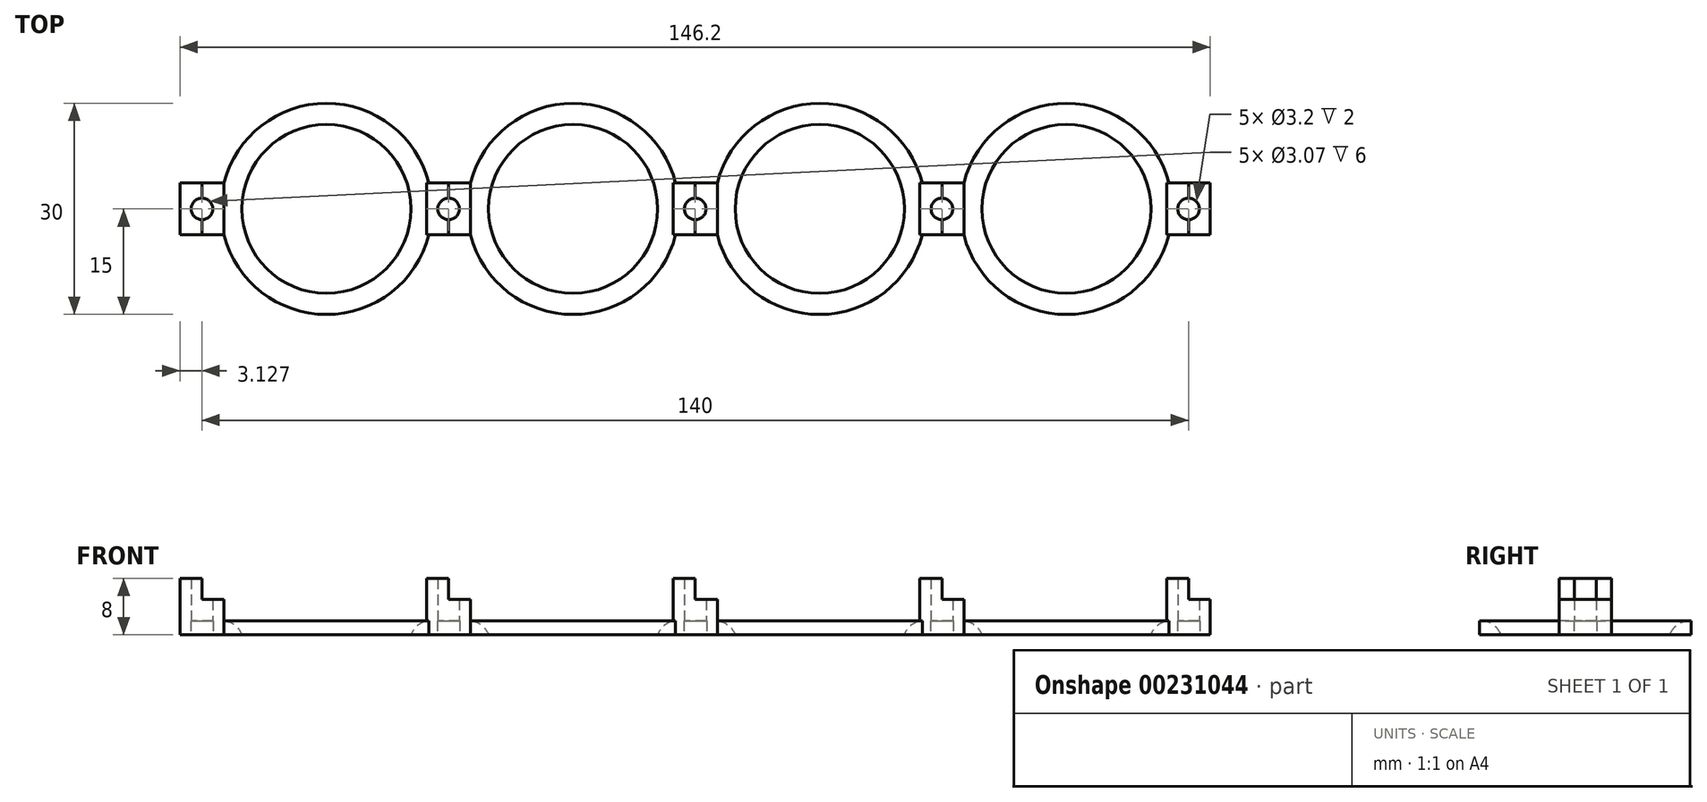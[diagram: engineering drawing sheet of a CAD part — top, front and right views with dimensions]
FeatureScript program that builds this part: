
annotation { "Feature Type Name" : "Feature", "Feature Type Description" : "" }
export const myFeature = defineFeature(function(context is Context, id is Id, definition is map)
    precondition{}
    {
        {
            var Q0;
            Q0=qCreatedBy(makeId("Top.planeOp"),FACE);
            var sketch = newSketch(context, id + "F0", { "sketchPlane" : qUnion([Q0])});
            skCircle(sketch, "E0", {"center": v(0, 0) * mm, "radius": 12 * mm});
            skArc(sketch, "E1", {"start": v(-14.54, -3.69) * mm, "mid": v(0, -15) * mm, "end": v(14.54, -3.69) * mm});
            skCircle(sketch, "E2.1.0.0", {"center": v(35, 0) * mm, "radius": 12 * mm});
            skArc(sketch, "E2.1.0.1", {"start": v(20.46, -3.69) * mm, "mid": v(35, -15) * mm, "end": v(49.54, -3.69) * mm});
            skCircle(sketch, "E2.2.0.0", {"center": v(70, 0) * mm, "radius": 12 * mm});
            skArc(sketch, "E2.2.0.1", {"start": v(55.46, -3.69) * mm, "mid": v(70, -15) * mm, "end": v(84.54, -3.69) * mm});
            skLineSegment(sketch, "E2.direction1", {"start": v(0, 0) * mm, "end": v(35, 0) * mm, "construction": true});
            skCircle(sketch, "E3.1.0.0", {"center": v(-35, 0) * mm, "radius": 12 * mm});
            skArc(sketch, "E3.1.0.1", {"start": v(-49.54, -3.69) * mm, "mid": v(-35, -15) * mm, "end": v(-20.46, -3.69) * mm});
            skLineSegment(sketch, "E3.direction1", {"start": v(0, 0) * mm, "end": v(-35, 0) * mm, "construction": true});
            skLineSegment(sketch, "E4.bottom", {"start": v(-49.54, 3.69) * mm, "end": v(-55.79, 3.69) * mm});
            skLineSegment(sketch, "E4.top", {"start": v(-49.54, -3.69) * mm, "end": v(-55.79, -3.69) * mm});
            skLineSegment(sketch, "E5.1.0.0", {"start": v(-14.54, -3.69) * mm, "end": v(-20.79, -3.69) * mm});
            skLineSegment(sketch, "E5.1.0.2", {"start": v(-14.54, 3.69) * mm, "end": v(-20.79, 3.69) * mm});
            skLineSegment(sketch, "E5.2.0.0", {"start": v(20.46, -3.69) * mm, "end": v(14.21, -3.69) * mm});
            skLineSegment(sketch, "E5.2.0.2", {"start": v(20.46, 3.69) * mm, "end": v(14.21, 3.69) * mm});
            skLineSegment(sketch, "E5.3.0.0", {"start": v(55.46, -3.69) * mm, "end": v(49.21, -3.69) * mm});
            skLineSegment(sketch, "E5.3.0.2", {"start": v(55.46, 3.69) * mm, "end": v(49.21, 3.69) * mm});
            skLineSegment(sketch, "E5.direction1", {"start": v(-55.79, -3.69) * mm, "end": v(-20.79, -3.69) * mm, "construction": true});
            skArc(sketch, "E6.trimOffspring", {"start": v(-20.46, 3.69) * mm, "mid": v(-35, 15) * mm, "end": v(-49.54, 3.69) * mm});
            skArc(sketch, "E7.trimOffspring", {"start": v(14.54, 3.69) * mm, "mid": v(0, 15) * mm, "end": v(-14.54, 3.69) * mm});
            skArc(sketch, "E8.trimOffspring", {"start": v(49.54, 3.69) * mm, "mid": v(35, 15) * mm, "end": v(20.46, 3.69) * mm});
            skLineSegment(sketch, "E9.0.4.0", {"start": v(90.46, -3.69) * mm, "end": v(84.21, -3.69) * mm});
            skLineSegment(sketch, "E9.6.4.0", {"start": v(90.46, 3.69) * mm, "end": v(84.21, 3.69) * mm});
            skLineSegment(sketch, "E10", {"start": v(-55.79, 3.69) * mm, "end": v(-55.79, -3.69) * mm});
            skArc(sketch, "E11.trimOffspring", {"start": v(84.54, 3.69) * mm, "mid": v(70, 15) * mm, "end": v(55.46, 3.69) * mm});
            skLineSegment(sketch, "E12", {"start": v(-55.79, 3.69) * mm, "end": v(-49.54, -3.69) * mm});
            skLineSegment(sketch, "E13", {"start": v(-49.54, 3.69) * mm, "end": v(-55.79, -3.69) * mm});
            skPoint(sketch, "E14", {"position": v(-52.66, 0) * mm});
            skCircle(sketch, "E15", {"center": v(-52.66, 0) * mm, "radius": 1.6 * mm});
            skCircle(sketch, "E16.1.0.0", {"center": v(-17.66, 0) * mm, "radius": 1.6 * mm});
            skCircle(sketch, "E16.2.0.0", {"center": v(17.34, 0) * mm, "radius": 1.6 * mm});
            skCircle(sketch, "E16.3.0.0", {"center": v(52.34, 0) * mm, "radius": 1.6 * mm});
            skCircle(sketch, "E16.4.0.0", {"center": v(87.34, 0) * mm, "radius": 1.6 * mm});
            skLineSegment(sketch, "E16.direction1", {"start": v(-52.66, 0) * mm, "end": v(-17.66, 0) * mm, "construction": true});
            skCircle(sketch, "E17.0.5.0", {"center": v(122.34, 0) * mm, "radius": 1.6 * mm});
            skLineSegment(sketch, "E18.0.5.0", {"start": v(125.46, -3.69) * mm, "end": v(119.21, -3.69) * mm});
            skLineSegment(sketch, "E18.6.5.0", {"start": v(125.46, 3.69) * mm, "end": v(119.21, 3.69) * mm});
            skCircle(sketch, "E19.0.3.0", {"center": v(105, 0) * mm, "radius": 12 * mm});
            skArc(sketch, "E19.2.3.0", {"start": v(90.46, -3.69) * mm, "mid": v(105, -15) * mm, "end": v(119.54, -3.69) * mm});
            skArc(sketch, "E20.trimOffspring", {"start": v(119.54, 3.69) * mm, "mid": v(105, 15) * mm, "end": v(90.46, 3.69) * mm});
            skLineSegment(sketch, "E21", {"start": v(125.46, 3.69) * mm, "end": v(125.46, -3.69) * mm});
            skSolve(sketch);
        }
        {
            var Q0;
            Q0=makeQuery(id+"F0.imprint","IMPRINT",FACE,{"disambiguationData":[TD([[makeQuery(id+"F0.imprint","IMPRINT",EDGE,{"derivedFrom":sQuery(id+"F0.wireOp",EDGE,"E0")}),-1.0]])]});
            var Q1;
            {var subQ0=sQuery(id+"F0.wireOp",EDGE,"E4.bottom");Q1=makeQuery(id+"F0.imprint","IMPRINT",FACE,{"disambiguationData":[TD([[makeQuery(id+"F0.imprint","IMPRINT",EDGE,{"derivedFrom":subQ0}),1.0]])]});}
            var Q2;
            {var subQ0=sQuery(id+"F0.wireOp",EDGE,"E10");Q2=makeQuery(id+"F0.imprint","IMPRINT",FACE,{"disambiguationData":[TD([[makeQuery(id+"F0.imprint","IMPRINT",EDGE,{"derivedFrom":subQ0}),1.0]])]});}
            var Q3;
            {var subQ0=sQuery(id+"F0.wireOp",EDGE,"E4.top");Q3=makeQuery(id+"F0.imprint","IMPRINT",FACE,{"disambiguationData":[TD([[makeQuery(id+"F0.imprint","IMPRINT",EDGE,{"derivedFrom":subQ0}),-1.0]])]});}
            extrude(context, id + "F1", {"entities" : qUnion([Q0, Q1, Q2, Q3]), "depth" : 2 * mm});
        }
        {
            var Q0;
            Q0=makeQuery(id+"F1.opExtrude","CAP_FACE",FACE,{"disambiguationData":[OSD([sQuery(id+"F0.wireOp",EDGE,"E0"),sQuery(id+"F0.wireOp",EDGE,"E1"),sQuery(id+"F0.wireOp",EDGE,"E2.1.0.0"),sQuery(id+"F0.wireOp",EDGE,"E2.1.0.1"),sQuery(id+"F0.wireOp",EDGE,"E2.2.0.0"),sQuery(id+"F0.wireOp",EDGE,"E2.2.0.1"),sQuery(id+"F0.wireOp",EDGE,"E3.1.0.0"),sQuery(id+"F0.wireOp",EDGE,"E3.1.0.1"),sQuery(id+"F0.wireOp",EDGE,"E4.bottom"),sQuery(id+"F0.wireOp",EDGE,"E4.top"),sQuery(id+"F0.wireOp",EDGE,"E5.1.0.0"),sQuery(id+"F0.wireOp",EDGE,"E5.1.0.2"),sQuery(id+"F0.wireOp",EDGE,"E5.2.0.0"),sQuery(id+"F0.wireOp",EDGE,"E5.2.0.2"),sQuery(id+"F0.wireOp",EDGE,"E5.3.0.0"),sQuery(id+"F0.wireOp",EDGE,"E5.3.0.2"),sQuery(id+"F0.wireOp",EDGE,"E6.trimOffspring"),sQuery(id+"F0.wireOp",EDGE,"E7.trimOffspring"),sQuery(id+"F0.wireOp",EDGE,"E8.trimOffspring"),sQuery(id+"F0.wireOp",EDGE,"E9.0.4.0"),sQuery(id+"F0.wireOp",EDGE,"E9.6.4.0"),sQuery(id+"F0.wireOp",EDGE,"E10"),sQuery(id+"F0.wireOp",EDGE,"8HqENXxz-xjcS-qaqN-4Ykx-RMen0NMMLaj5"),sQuery(id+"F0.wireOp",EDGE,"E11.trimOffspring"),sQuery(id+"F0.wireOp",EDGE,"E15"),sQuery(id+"F0.wireOp",EDGE,"E16.1.0.0"),sQuery(id+"F0.wireOp",EDGE,"E16.2.0.0"),sQuery(id+"F0.wireOp",EDGE,"E16.3.0.0"),sQuery(id+"F0.wireOp",EDGE,"E16.4.0.0")])],"isStart":false});
            var sketch = newSketch(context, id + "F2", { "sketchPlane" : qUnion([Q0])});
            skLineSegment(sketch, "E22.bottom", {"start": v(-55.79, 3.69) * mm, "end": v(-49.54, 3.69) * mm});
            skLineSegment(sketch, "E22.top", {"start": v(-55.79, -3.69) * mm, "end": v(-49.54, -3.69) * mm});
            skLineSegment(sketch, "E22.left", {"start": v(-55.79, 3.69) * mm, "end": v(-55.79, -3.69) * mm});
            skLineSegment(sketch, "E22.right", {"start": v(-49.54, 3.69) * mm, "end": v(-49.54, -3.69) * mm});
            skCircle(sketch, "E23", {"center": v(-52.66, 0) * mm, "radius": 1.54 * mm});
            skLineSegment(sketch, "E24.1.0.0", {"start": v(-14.54, 3.69) * mm, "end": v(-14.54, -3.69) * mm});
            skLineSegment(sketch, "E24.1.0.1", {"start": v(-20.79, 3.69) * mm, "end": v(-14.54, 3.69) * mm});
            skLineSegment(sketch, "E24.1.0.2", {"start": v(-20.79, 3.69) * mm, "end": v(-20.79, -3.69) * mm});
            skLineSegment(sketch, "E24.1.0.3", {"start": v(-20.79, -3.69) * mm, "end": v(-14.54, -3.69) * mm});
            skCircle(sketch, "E24.1.0.4", {"center": v(-17.66, 0) * mm, "radius": 1.54 * mm});
            skLineSegment(sketch, "E24.2.0.0", {"start": v(20.46, 3.69) * mm, "end": v(20.46, -3.69) * mm});
            skLineSegment(sketch, "E24.2.0.1", {"start": v(14.21, 3.69) * mm, "end": v(20.46, 3.69) * mm});
            skLineSegment(sketch, "E24.2.0.2", {"start": v(14.21, 3.69) * mm, "end": v(14.21, -3.69) * mm});
            skLineSegment(sketch, "E24.2.0.3", {"start": v(14.21, -3.69) * mm, "end": v(20.46, -3.69) * mm});
            skCircle(sketch, "E24.2.0.4", {"center": v(17.34, 0) * mm, "radius": 1.54 * mm});
            skLineSegment(sketch, "E24.3.0.0", {"start": v(55.46, 3.69) * mm, "end": v(55.46, -3.69) * mm});
            skLineSegment(sketch, "E24.3.0.1", {"start": v(49.21, 3.69) * mm, "end": v(55.46, 3.69) * mm});
            skLineSegment(sketch, "E24.3.0.2", {"start": v(49.21, 3.69) * mm, "end": v(49.21, -3.69) * mm});
            skLineSegment(sketch, "E24.3.0.3", {"start": v(49.21, -3.69) * mm, "end": v(55.46, -3.69) * mm});
            skCircle(sketch, "E24.3.0.4", {"center": v(52.34, 0) * mm, "radius": 1.54 * mm});
            skLineSegment(sketch, "E24.4.0.0", {"start": v(90.46, 3.69) * mm, "end": v(90.46, -3.69) * mm});
            skLineSegment(sketch, "E24.4.0.1", {"start": v(84.21, 3.69) * mm, "end": v(90.46, 3.69) * mm});
            skLineSegment(sketch, "E24.4.0.2", {"start": v(84.21, 3.69) * mm, "end": v(84.21, -3.69) * mm});
            skLineSegment(sketch, "E24.4.0.3", {"start": v(84.21, -3.69) * mm, "end": v(90.46, -3.69) * mm});
            skCircle(sketch, "E24.4.0.4", {"center": v(87.34, 0) * mm, "radius": 1.54 * mm});
            skLineSegment(sketch, "E24.direction1", {"start": v(-49.54, -3.69) * mm, "end": v(-14.54, -3.69) * mm, "construction": true});
            skLineSegment(sketch, "E25.0.5.0", {"start": v(125.46, 3.69) * mm, "end": v(125.46, -3.69) * mm});
            skLineSegment(sketch, "E25.3.5.0", {"start": v(119.21, 3.69) * mm, "end": v(125.46, 3.69) * mm});
            skLineSegment(sketch, "E25.6.5.0", {"start": v(119.21, 3.69) * mm, "end": v(119.21, -3.69) * mm});
            skLineSegment(sketch, "E25.9.5.0", {"start": v(119.21, -3.69) * mm, "end": v(125.46, -3.69) * mm});
            skCircle(sketch, "E25.12.5.0", {"center": v(122.34, 0) * mm, "radius": 1.54 * mm});
            skSolve(sketch);
        }
        {
            var Q0;
            Q0 = qSketchRegion(id + "F2", true);
            extrude(context, id + "F3", {"entities" : qUnion([Q0]), "operationType" : NewBodyOperationType.ADD, "depth" : 6 * mm});
        }
        {
            var Q0;
            Q0=makeQuery(id+"F3.boolean.opBoolean","MERGE",FACE,{"derivedFrom":[makeQuery(id+"F1.opExtrude","SWEPT_FACE",FACE,{"disambiguationData":[OSD([sQuery(id+"F0.wireOp",EDGE,"E4.top")])]}),makeQuery(id+"F3.opExtrude","SWEPT_FACE",FACE,{"disambiguationData":[OSD([sQuery(id+"F2.wireOp",EDGE,"E22.top")])]})]});
            var sketch = newSketch(context, id + "F4", { "sketchPlane" : qUnion([Q0])});
            skLineSegment(sketch, "E26", {"start": v(-52.66, 8) * mm, "end": v(-52.66, 0) * mm});
            skLineSegment(sketch, "E27", {"start": v(-49.54, 5) * mm, "end": v(-52.66, 5) * mm});
            skLineSegment(sketch, "E28", {"start": v(-52.66, 8) * mm, "end": v(-49.54, 8) * mm});
            skLineSegment(sketch, "E29", {"start": v(-49.54, 8) * mm, "end": v(-49.54, 5) * mm});
            skLineSegment(sketch, "E30.1.0.0", {"start": v(-14.54, 5) * mm, "end": v(-17.66, 5) * mm});
            skLineSegment(sketch, "E30.1.0.1", {"start": v(-14.54, 8) * mm, "end": v(-14.54, 5) * mm});
            skLineSegment(sketch, "E30.1.0.2", {"start": v(-17.66, 8) * mm, "end": v(-14.54, 8) * mm});
            skLineSegment(sketch, "E30.1.0.3", {"start": v(-17.66, 8) * mm, "end": v(-17.66, 0) * mm});
            skLineSegment(sketch, "E30.2.0.0", {"start": v(20.46, 5) * mm, "end": v(17.34, 5) * mm});
            skLineSegment(sketch, "E30.2.0.1", {"start": v(20.46, 8) * mm, "end": v(20.46, 5) * mm});
            skLineSegment(sketch, "E30.2.0.2", {"start": v(17.34, 8) * mm, "end": v(20.46, 8) * mm});
            skLineSegment(sketch, "E30.2.0.3", {"start": v(17.34, 8) * mm, "end": v(17.34, 0) * mm});
            skLineSegment(sketch, "E30.3.0.0", {"start": v(55.46, 5) * mm, "end": v(52.34, 5) * mm});
            skLineSegment(sketch, "E30.3.0.1", {"start": v(55.46, 8) * mm, "end": v(55.46, 5) * mm});
            skLineSegment(sketch, "E30.3.0.2", {"start": v(52.34, 8) * mm, "end": v(55.46, 8) * mm});
            skLineSegment(sketch, "E30.3.0.3", {"start": v(52.34, 8) * mm, "end": v(52.34, 0) * mm});
            skLineSegment(sketch, "E30.4.0.0", {"start": v(90.46, 5) * mm, "end": v(87.34, 5) * mm});
            skLineSegment(sketch, "E30.4.0.1", {"start": v(90.46, 8) * mm, "end": v(90.46, 5) * mm});
            skLineSegment(sketch, "E30.4.0.2", {"start": v(87.34, 8) * mm, "end": v(90.46, 8) * mm});
            skLineSegment(sketch, "E30.4.0.3", {"start": v(87.34, 8) * mm, "end": v(87.34, 0) * mm});
            skLineSegment(sketch, "E30.direction1", {"start": v(-52.66, 5) * mm, "end": v(-17.66, 5) * mm, "construction": true});
            skLineSegment(sketch, "E31.0.5.0", {"start": v(125.46, 5) * mm, "end": v(122.34, 5) * mm});
            skLineSegment(sketch, "E31.3.5.0", {"start": v(125.46, 8) * mm, "end": v(125.46, 5) * mm});
            skLineSegment(sketch, "E31.6.5.0", {"start": v(122.34, 8) * mm, "end": v(125.46, 8) * mm});
            skLineSegment(sketch, "E31.9.5.0", {"start": v(122.34, 8) * mm, "end": v(122.34, 0) * mm});
            skSolve(sketch);
        }
        {
            var Q0;
            {var subQ2=sQuery(id+"F4.wireOp",EDGE,"E27");Q0=makeQuery(id+"F4.imprint","IMPRINT",FACE,{"disambiguationData":[TD([[makeQuery(id+"F4.imprint","IMPRINT",EDGE,{"derivedFrom":subQ2}),-1.0]])]});}
            var Q1;
            {var subQ0=sQuery(id+"F4.wireOp",EDGE,"E30.1.0.0");Q1=makeQuery(id+"F4.imprint","IMPRINT",FACE,{"disambiguationData":[TD([[makeQuery(id+"F4.imprint","IMPRINT",EDGE,{"derivedFrom":subQ0}),-1.0]])]});}
            var Q2;
            {var subQ0=sQuery(id+"F4.wireOp",EDGE,"E30.2.0.0");Q2=makeQuery(id+"F4.imprint","IMPRINT",FACE,{"disambiguationData":[TD([[makeQuery(id+"F4.imprint","IMPRINT",EDGE,{"derivedFrom":subQ0}),-1.0]])]});}
            var Q3;
            {var subQ0=sQuery(id+"F4.wireOp",EDGE,"E30.3.0.0");Q3=makeQuery(id+"F4.imprint","IMPRINT",FACE,{"disambiguationData":[TD([[makeQuery(id+"F4.imprint","IMPRINT",EDGE,{"derivedFrom":subQ0}),-1.0]])]});}
            var Q4;
            {var subQ0=sQuery(id+"F4.wireOp",EDGE,"E30.4.0.0");Q4=makeQuery(id+"F4.imprint","IMPRINT",FACE,{"disambiguationData":[TD([[makeQuery(id+"F4.imprint","IMPRINT",EDGE,{"derivedFrom":subQ0}),-1.0]])]});}
            var Q5;
            {var subQ0=sQuery(id+"F4.wireOp",EDGE,"E31.0.5.0");Q5=makeQuery(id+"F4.imprint","IMPRINT",FACE,{"disambiguationData":[TD([[makeQuery(id+"F4.imprint","IMPRINT",EDGE,{"derivedFrom":subQ0}),-1.0]])]});}
            extrude(context, id + "F5", {"entities" : qUnion([Q0, Q1, Q2, Q3, Q4, Q5]), "operationType" : NewBodyOperationType.REMOVE, "endBound" : BoundingType.THROUGH_ALL, "oppositeDirection" : true, "depth" : 25 * mm});
        }
        {
            var Q0;
            Q0=makeQuery(id+"F1.opExtrude","CAP_EDGE",EDGE,{"disambiguationData":[OSD([sQuery(id+"F0.wireOp",EDGE,"E3.1.0.0")])],"isStart":false});
            var Q1;
            Q1=makeQuery(id+"F1.opExtrude","CAP_EDGE",EDGE,{"disambiguationData":[OSD([sQuery(id+"F0.wireOp",EDGE,"E0")])],"isStart":false});
            var Q2;
            Q2=makeQuery(id+"F1.opExtrude","CAP_EDGE",EDGE,{"disambiguationData":[OSD([sQuery(id+"F0.wireOp",EDGE,"E2.1.0.0")])],"isStart":false});
            var Q3;
            Q3=makeQuery(id+"F1.opExtrude","CAP_EDGE",EDGE,{"disambiguationData":[OSD([sQuery(id+"F0.wireOp",EDGE,"E2.2.0.0")])],"isStart":false});
            var Q4;
            Q4=makeQuery(id+"F1.opExtrude","CAP_EDGE",EDGE,{"disambiguationData":[OSD([sQuery(id+"F0.wireOp",EDGE,"E19.0.3.0")])],"isStart":false});
            fillet(context, id + "F6", {"entities" : qUnion([Q0, Q1, Q2, Q3, Q4]), "radius" : 3 * mm, "tangentPropagation" : true, "allowEdgeOverflow" : false});
        }
        {
            var Q0;
            Q0=qCreatedBy(makeId("Top.planeOp"),FACE);
            var sketch = newSketch(context, id + "F7", { "sketchPlane" : qUnion([Q0])});
            skLineSegment(sketch, "E32", {"start": v(90.4, 3.9) * mm, "end": v(90.4, -4.8) * mm});
            skLineSegment(sketch, "E33", {"start": v(90.4, -4.8) * mm, "end": v(90.4, -19.6) * mm});
            skLineSegment(sketch, "E34.bottom", {"start": v(90.4, -19.6) * mm, "end": v(130.76, -19.6) * mm});
            skLineSegment(sketch, "E34.top", {"start": v(90.4, 20.04) * mm, "end": v(130.76, 20.04) * mm});
            skLineSegment(sketch, "E34.left", {"start": v(90.4, -19.6) * mm, "end": v(90.4, 20.04) * mm});
            skLineSegment(sketch, "E34.right", {"start": v(130.76, -19.6) * mm, "end": v(130.76, 20.04) * mm});
            skSolve(sketch);
        }
        {
            var Q0;
            {var subQ0=sQuery(id+"F7.wireOp",EDGE,"E34.bottom");Q0=makeQuery(id+"F7.imprint","IMPRINT",FACE,{"disambiguationData":[TD([[makeQuery(id+"F7.imprint","IMPRINT",EDGE,{"derivedFrom":subQ0}),1.0]])]});}
            extrude(context, id + "F8", {"entities" : qUnion([Q0]), "operationType" : NewBodyOperationType.REMOVE, "endBound" : BoundingType.THROUGH_ALL, "depth" : 25 * mm});
        }
    });
